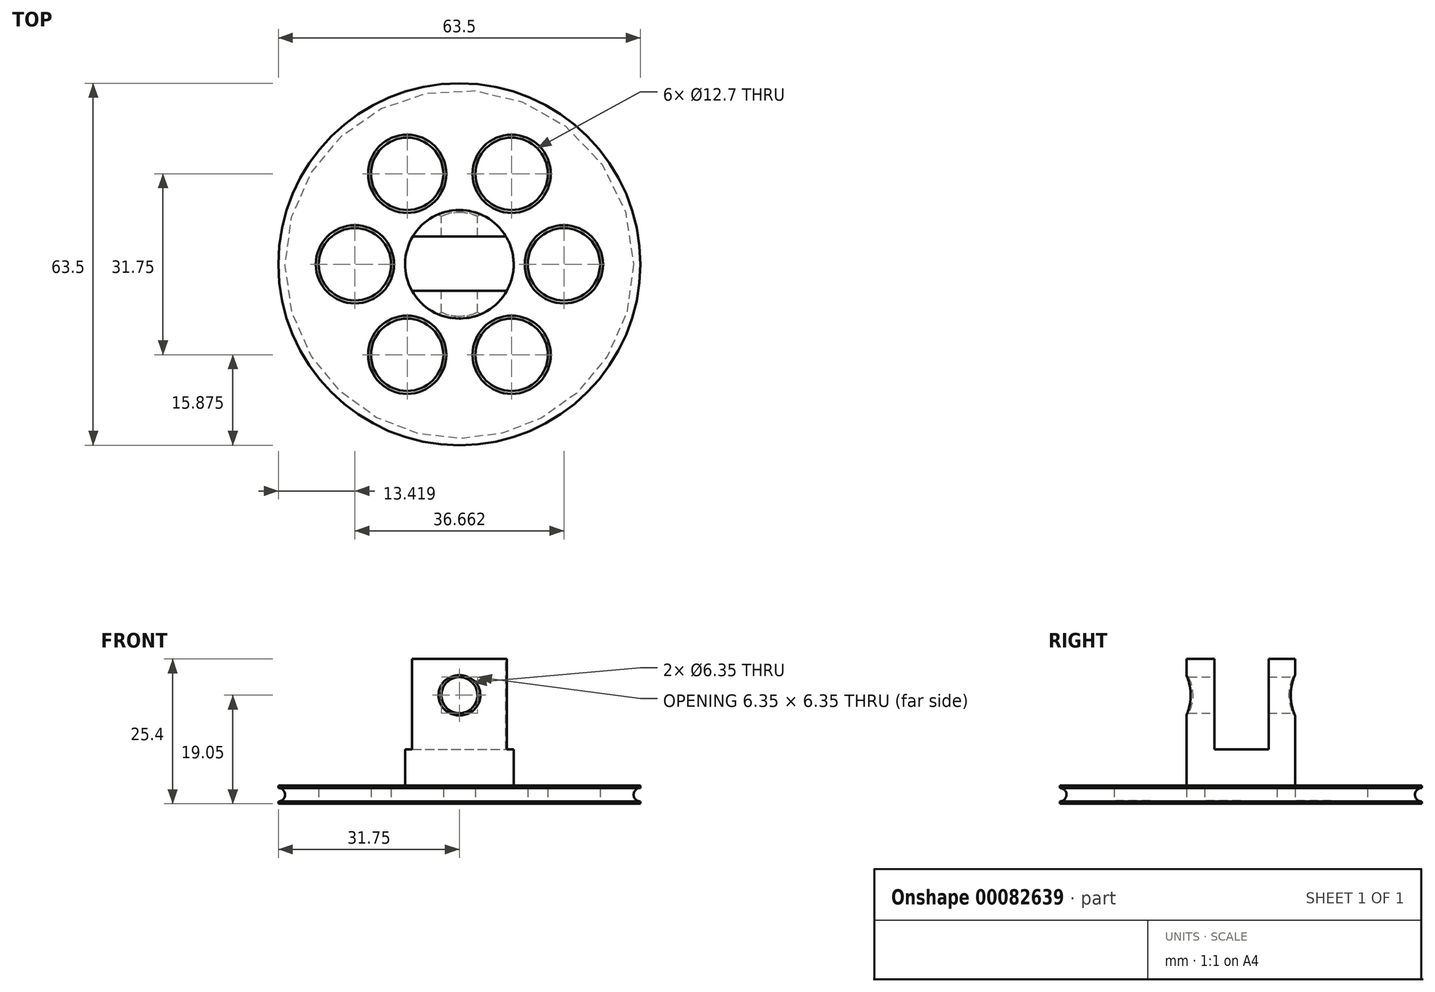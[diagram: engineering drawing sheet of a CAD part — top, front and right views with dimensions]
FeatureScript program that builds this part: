
annotation { "Feature Type Name" : "Feature", "Feature Type Description" : "" }
export const myFeature = defineFeature(function(context is Context, id is Id, definition is map)
    precondition{}
    {
        {
            var Q0;
            Q0=qCreatedBy(makeId("Front.planeOp"),FACE);
            var sketch = newSketch(context, id + "F0", { "sketchPlane" : qUnion([Q0])});
            skLineSegment(sketch, "E0", {"start": v(0, 0) * mm, "end": v(-31.75, 0) * mm});
            skLineSegment(sketch, "E1", {"start": v(-31.75, 0) * mm, "end": v(-31.75, 0.4) * mm});
            skLineSegment(sketch, "E2", {"start": v(-31.75, 3.17) * mm, "end": v(-9.52, 3.17) * mm});
            skLineSegment(sketch, "E3", {"start": v(-9.52, 3.17) * mm, "end": v(-9.53, 25.4) * mm});
            skLineSegment(sketch, "E4", {"start": v(-9.53, 25.4) * mm, "end": v(0, 25.4) * mm});
            skLineSegment(sketch, "E5", {"start": v(0, 25.4) * mm, "end": v(0, 0) * mm});
            skPoint(sketch, "E6", {"position": v(-31.75, 1.59) * mm});
            skPoint(sketch, "E7", {"position": v(-13.47, -20.17) * mm});
            skArc(sketch, "E8", {"start": v(-31.75, 0.4) * mm, "mid": v(-30.57, 1.59) * mm, "end": v(-31.75, 2.77) * mm});
            skLineSegment(sketch, "E9.trimOffspring", {"start": v(-31.75, 2.77) * mm, "end": v(-31.75, 3.17) * mm});
            skSolve(sketch);
        }
        {
            var Q0;
            Q0=makeQuery(id+"F0.imprint","IMPRINT",FACE,{"disambiguationData":[TD([[makeQuery(id+"F0.imprint","IMPRINT",EDGE,{"derivedFrom":sQuery(id+"F0.wireOp",EDGE,"E0")}),-1.0]])]});
            var Q1;
            Q1=sQuery(id+"F0.wireOp",EDGE,"E5");
            revolve(context, id + "F1", {"entities" : qUnion([Q0]), "axis" : qUnion([Q1]), "revolveType" : RevolveType.FULL});
        }
        {
            var Q0;
            Q0=qCreatedBy(makeId("Right.planeOp"),FACE);
            var sketch = newSketch(context, id + "F2", { "sketchPlane" : qUnion([Q0])});
            skLineSegment(sketch, "E10.bottom", {"start": v(-4.62, 31.75) * mm, "end": v(4.9, 31.75) * mm});
            skLineSegment(sketch, "E10.top", {"start": v(-4.62, 9.52) * mm, "end": v(4.9, 9.52) * mm});
            skLineSegment(sketch, "E10.left", {"start": v(-4.62, 31.75) * mm, "end": v(-4.62, 9.52) * mm});
            skLineSegment(sketch, "E10.right", {"start": v(4.9, 31.75) * mm, "end": v(4.9, 9.52) * mm});
            skSolve(sketch);
        }
        {
            var Q0;
            Q0 = qSketchRegion(id + "F2", true);
            extrude(context, id + "F3", {"entities" : qUnion([Q0]), "operationType" : NewBodyOperationType.REMOVE, "endBound" : BoundingType.SYMMETRIC, "oppositeDirection" : true, "depth" : 25.4 * mm});
        }
        {
            var Q0;
            Q0=qCreatedBy(makeId("Front.planeOp"),FACE);
            var sketch = newSketch(context, id + "F4", { "sketchPlane" : qUnion([Q0])});
            skPoint(sketch, "E11", {"position": v(0, 19.05) * mm});
            skCircle(sketch, "E12", {"center": v(0, 19.05) * mm, "radius": 3.18 * mm});
            skSolve(sketch);
        }
        {
            var Q0;
            Q0 = qSketchRegion(id + "F4", true);
            extrude(context, id + "F5", {"entities" : qUnion([Q0]), "operationType" : NewBodyOperationType.REMOVE, "endBound" : BoundingType.SYMMETRIC, "depth" : 25.4 * mm});
        }
        {
            var Q0;
            Q0=makeQuery(id+"F5.boolean.opBoolean","INTERSECT",EDGE,{"disambiguationData":[OD(0.0)],"derivedFrom":[makeQuery(id+"F1.opRevolve","SWEPT_FACE",FACE,{"disambiguationData":[OSD([sQuery(id+"F0.wireOp",EDGE,"E3")])]}),makeQuery(id+"F5.opExtrude","SWEPT_FACE",FACE,{"disambiguationData":[OSD([sQuery(id+"F4.wireOp",EDGE,"E12")])]})]});
            var Q1;
            Q1=makeQuery(id+"F5.boolean.opBoolean","INTERSECT",EDGE,{"disambiguationData":[OD(1.0)],"derivedFrom":[makeQuery(id+"F1.opRevolve","SWEPT_FACE",FACE,{"disambiguationData":[OSD([sQuery(id+"F0.wireOp",EDGE,"E3")])]}),makeQuery(id+"F5.opExtrude","SWEPT_FACE",FACE,{"disambiguationData":[OSD([sQuery(id+"F4.wireOp",EDGE,"E12")])]})]});
            chamfer(context, id + "F6", {"entities" : qUnion([Q0, Q1]), "width" : 0.38 * mm, "tangentPropagation" : true});
        }
        {
            var Q0;
            Q0=makeQuery(id+"F1.opRevolve","SWEPT_FACE",FACE,{"disambiguationData":[OSD([sQuery(id+"F0.wireOp",EDGE,"E2")])]});
            var sketch = newSketch(context, id + "F7", { "sketchPlane" : qUnion([Q0])});
            skPoint(sketch, "E13.0.midPoint", {"position": v(0, 15.88) * mm});
            skCircle(sketch, "E14", {"center": v(-9.17, 15.88) * mm, "radius": 6.35 * mm});
            skCircle(sketch, "E15", {"center": v(9.17, 15.88) * mm, "radius": 6.35 * mm});
            skCircle(sketch, "E16", {"center": v(18.33, 0) * mm, "radius": 6.35 * mm});
            skCircle(sketch, "E17", {"center": v(9.17, -15.88) * mm, "radius": 6.35 * mm});
            skCircle(sketch, "E18", {"center": v(-9.17, -15.88) * mm, "radius": 6.35 * mm});
            skCircle(sketch, "E19", {"center": v(-18.33, 0) * mm, "radius": 6.35 * mm});
            skSolve(sketch);
        }
        {
            var Q0;
            Q0 = qSketchRegion(id + "F7", true);
            extrude(context, id + "F8", {"entities" : qUnion([Q0]), "operationType" : NewBodyOperationType.REMOVE, "endBound" : BoundingType.SYMMETRIC, "depth" : 25.4 * mm});
        }
        {
            var Q0;
            Q0=makeQuery(id+"F8.boolean.opBoolean","INTERSECT",EDGE,{"derivedFrom":[makeQuery(id+"F1.opRevolve","SWEPT_FACE",FACE,{"disambiguationData":[OSD([sQuery(id+"F0.wireOp",EDGE,"E0")])]}),makeQuery(id+"F8.opExtrude","SWEPT_FACE",FACE,{"disambiguationData":[OSD([sQuery(id+"F7.wireOp",EDGE,"E14")])]})]});
            var Q1;
            Q1=makeQuery(id+"F8.boolean.opBoolean","INTERSECT",EDGE,{"derivedFrom":[makeQuery(id+"F1.opRevolve","SWEPT_FACE",FACE,{"disambiguationData":[OSD([sQuery(id+"F0.wireOp",EDGE,"E0")])]}),makeQuery(id+"F8.opExtrude","SWEPT_FACE",FACE,{"disambiguationData":[OSD([sQuery(id+"F7.wireOp",EDGE,"E15")])]})]});
            var Q2;
            Q2=makeQuery(id+"F8.boolean.opBoolean","INTERSECT",EDGE,{"derivedFrom":[makeQuery(id+"F1.opRevolve","SWEPT_FACE",FACE,{"disambiguationData":[OSD([sQuery(id+"F0.wireOp",EDGE,"E2")])]}),makeQuery(id+"F8.opExtrude","SWEPT_FACE",FACE,{"disambiguationData":[OSD([sQuery(id+"F7.wireOp",EDGE,"E16")])]})]});
            var Q3;
            Q3=makeQuery(id+"F8.boolean.opBoolean","INTERSECT",EDGE,{"derivedFrom":[makeQuery(id+"F1.opRevolve","SWEPT_FACE",FACE,{"disambiguationData":[OSD([sQuery(id+"F0.wireOp",EDGE,"E0")])]}),makeQuery(id+"F8.opExtrude","SWEPT_FACE",FACE,{"disambiguationData":[OSD([sQuery(id+"F7.wireOp",EDGE,"E17")])]})]});
            var Q4;
            Q4=makeQuery(id+"F8.boolean.opBoolean","INTERSECT",EDGE,{"derivedFrom":[makeQuery(id+"F1.opRevolve","SWEPT_FACE",FACE,{"disambiguationData":[OSD([sQuery(id+"F0.wireOp",EDGE,"E2")])]}),makeQuery(id+"F8.opExtrude","SWEPT_FACE",FACE,{"disambiguationData":[OSD([sQuery(id+"F7.wireOp",EDGE,"E18")])]})]});
            var Q5;
            Q5=makeQuery(id+"F8.boolean.opBoolean","INTERSECT",EDGE,{"derivedFrom":[makeQuery(id+"F1.opRevolve","SWEPT_FACE",FACE,{"disambiguationData":[OSD([sQuery(id+"F0.wireOp",EDGE,"E2")])]}),makeQuery(id+"F8.opExtrude","SWEPT_FACE",FACE,{"disambiguationData":[OSD([sQuery(id+"F7.wireOp",EDGE,"E19")])]})]});
            var Q6;
            Q6=makeQuery(id+"F8.boolean.opBoolean","INTERSECT",EDGE,{"derivedFrom":[makeQuery(id+"F1.opRevolve","SWEPT_FACE",FACE,{"disambiguationData":[OSD([sQuery(id+"F0.wireOp",EDGE,"E0")])]}),makeQuery(id+"F8.opExtrude","SWEPT_FACE",FACE,{"disambiguationData":[OSD([sQuery(id+"F7.wireOp",EDGE,"E16")])]})]});
            var Q7;
            Q7=makeQuery(id+"F8.boolean.opBoolean","INTERSECT",EDGE,{"derivedFrom":[makeQuery(id+"F1.opRevolve","SWEPT_FACE",FACE,{"disambiguationData":[OSD([sQuery(id+"F0.wireOp",EDGE,"E2")])]}),makeQuery(id+"F8.opExtrude","SWEPT_FACE",FACE,{"disambiguationData":[OSD([sQuery(id+"F7.wireOp",EDGE,"E14")])]})]});
            var Q8;
            Q8=makeQuery(id+"F8.boolean.opBoolean","INTERSECT",EDGE,{"derivedFrom":[makeQuery(id+"F1.opRevolve","SWEPT_FACE",FACE,{"disambiguationData":[OSD([sQuery(id+"F0.wireOp",EDGE,"E0")])]}),makeQuery(id+"F8.opExtrude","SWEPT_FACE",FACE,{"disambiguationData":[OSD([sQuery(id+"F7.wireOp",EDGE,"E19")])]})]});
            var Q9;
            Q9=makeQuery(id+"F8.boolean.opBoolean","INTERSECT",EDGE,{"derivedFrom":[makeQuery(id+"F1.opRevolve","SWEPT_FACE",FACE,{"disambiguationData":[OSD([sQuery(id+"F0.wireOp",EDGE,"E0")])]}),makeQuery(id+"F8.opExtrude","SWEPT_FACE",FACE,{"disambiguationData":[OSD([sQuery(id+"F7.wireOp",EDGE,"E18")])]})]});
            var Q10;
            Q10=makeQuery(id+"F8.boolean.opBoolean","INTERSECT",EDGE,{"derivedFrom":[makeQuery(id+"F1.opRevolve","SWEPT_FACE",FACE,{"disambiguationData":[OSD([sQuery(id+"F0.wireOp",EDGE,"E2")])]}),makeQuery(id+"F8.opExtrude","SWEPT_FACE",FACE,{"disambiguationData":[OSD([sQuery(id+"F7.wireOp",EDGE,"E17")])]})]});
            var Q11;
            Q11=makeQuery(id+"F8.boolean.opBoolean","INTERSECT",EDGE,{"derivedFrom":[makeQuery(id+"F1.opRevolve","SWEPT_FACE",FACE,{"disambiguationData":[OSD([sQuery(id+"F0.wireOp",EDGE,"E2")])]}),makeQuery(id+"F8.opExtrude","SWEPT_FACE",FACE,{"disambiguationData":[OSD([sQuery(id+"F7.wireOp",EDGE,"E15")])]})]});
            chamfer(context, id + "F9", {"entities" : qUnion([Q0, Q1, Q2, Q3, Q4, Q5, Q6, Q7, Q8, Q9, Q10, Q11]), "width" : 0.5 * mm, "tangentPropagation" : true});
        }
    });
